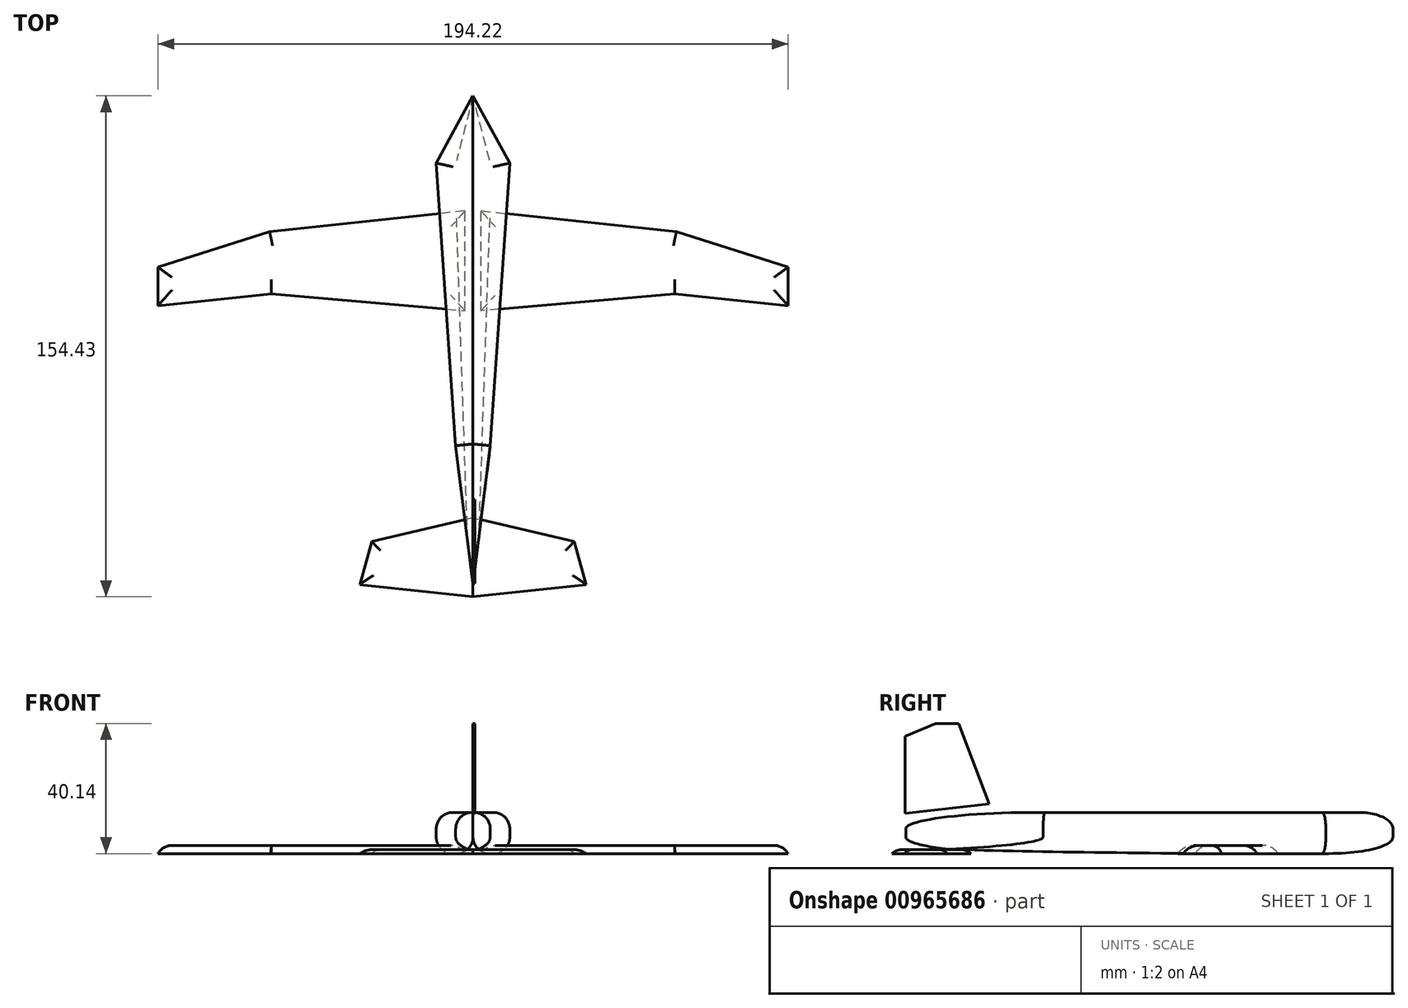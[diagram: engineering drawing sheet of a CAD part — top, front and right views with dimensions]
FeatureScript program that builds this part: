
annotation { "Feature Type Name" : "Feature", "Feature Type Description" : "" }
export const myFeature = defineFeature(function(context is Context, id is Id, definition is map)
    precondition{}
    {
        {
            var Q0;
            Q0=qCreatedBy(makeId("Top.planeOp"),FACE);
            var sketch = newSketch(context, id + "F0", { "sketchPlane" : qUnion([Q0])});
            skLineSegment(sketch, "E0", {"start": v(0, 25.84) * mm, "end": v(62.67, 19.1) * mm});
            skLineSegment(sketch, "E1", {"start": v(62.67, 19.1) * mm, "end": v(97.11, 8.22) * mm});
            skLineSegment(sketch, "E2", {"start": v(97.11, 8.22) * mm, "end": v(97.11, -3.66) * mm});
            skLineSegment(sketch, "E3", {"start": v(97.11, -3.66) * mm, "end": v(62.13, 0) * mm});
            skLineSegment(sketch, "E4", {"start": v(62.13, 0) * mm, "end": v(2.44, -5.26) * mm});
            skLineSegment(sketch, "E5", {"start": v(2.44, -5.26) * mm, "end": v(2.44, 25.84) * mm});
            skSolve(sketch);
        }
        {
            var Q0;
            {var subQ0=sQuery(id+"F0.wireOp",EDGE,"E1");Q0=makeQuery(id+"F0.imprint","IMPRINT",FACE,{"disambiguationData":[TD([[makeQuery(id+"F0.imprint","IMPRINT",EDGE,{"derivedFrom":subQ0}),-1.0]])]});}
            extrude(context, id + "F1", {"entities" : qUnion([Q0]), "depth" : 2.54 * mm, "offsetDistance" : 25.4 * mm});
        }
        {
            var Q0;
            Q0=makeQuery(id+"F1.opExtrude","CAP_EDGE",EDGE,{"disambiguationData":[OSD([sQuery(id+"F0.wireOp",EDGE,"E2")])],"isStart":false});
            var Q1;
            Q1=makeQuery(id+"F1.opExtrude","CAP_EDGE",EDGE,{"disambiguationData":[OSD([sQuery(id+"F0.wireOp",EDGE,"E1")])],"isStart":false});
            var Q2;
            Q2=makeQuery(id+"F1.opExtrude","CAP_FACE",FACE,{"disambiguationData":[OSD([sQuery(id+"F0.wireOp",EDGE,"E0"),sQuery(id+"F0.wireOp",EDGE,"E1"),sQuery(id+"F0.wireOp",EDGE,"E2"),sQuery(id+"F0.wireOp",EDGE,"E3"),sQuery(id+"F0.wireOp",EDGE,"E4"),sQuery(id+"F0.wireOp",EDGE,"E5")])],"isStart":false});
            fillet(context, id + "F2", {"entities" : qUnion([Q0, Q1, Q2]), "radius" : 5.08 * mm, "tangentPropagation" : true, "allowEdgeOverflow" : false});
        }
        {
            var Q0;
            Q0=qCreatedBy(makeId("Top.planeOp"),FACE);
            var sketch = newSketch(context, id + "F3", { "sketchPlane" : qUnion([Q0])});
            skLineSegment(sketch, "E6", {"start": v(0, -69.07) * mm, "end": v(31.2, -76.35) * mm});
            skLineSegment(sketch, "E7", {"start": v(31.2, -76.35) * mm, "end": v(34.91, -89.64) * mm});
            skLineSegment(sketch, "E8", {"start": v(34.91, -89.64) * mm, "end": v(0, -93.44) * mm});
            skLineSegment(sketch, "E9", {"start": v(0, -93.44) * mm, "end": v(0, -69.07) * mm});
            skSolve(sketch);
        }
        {
            var Q0;
            Q0=makeQuery(id+"F3.imprint","IMPRINT",FACE,{"disambiguationData":[TD([[makeQuery(id+"F3.imprint","IMPRINT",EDGE,{"derivedFrom":sQuery(id+"F3.wireOp",EDGE,"E6")}),-1.0]])]});
            extrude(context, id + "F4", {"entities" : qUnion([Q0]), "depth" : 1.27 * mm, "offsetDistance" : 25.4 * mm});
        }
        {
            var Q0;
            Q0=makeQuery(id+"F4.opExtrude","CAP_EDGE",EDGE,{"disambiguationData":[OSD([sQuery(id+"F3.wireOp",EDGE,"E7")])],"isStart":false});
            var Q1;
            Q1=makeQuery(id+"F4.opExtrude","CAP_EDGE",EDGE,{"disambiguationData":[OSD([sQuery(id+"F3.wireOp",EDGE,"E6")])],"isStart":false});
            var Q2;
            Q2=makeQuery(id+"F4.opExtrude","CAP_EDGE",EDGE,{"disambiguationData":[OSD([sQuery(id+"F3.wireOp",EDGE,"E8")])],"isStart":false});
            fillet(context, id + "F5", {"entities" : qUnion([Q0, Q1, Q2]), "radius" : 5.08 * mm, "tangentPropagation" : true, "allowEdgeOverflow" : false});
        }
        {
            var Q0;
            Q0=makeQuery(id+"F4.opExtrude","SWEPT_BODY",BODY,{"disambiguationData":[OSD([sQuery(id+"F3.wireOp",EDGE,"E6"),sQuery(id+"F3.wireOp",EDGE,"E7"),sQuery(id+"F3.wireOp",EDGE,"E8"),sQuery(id+"F3.wireOp",EDGE,"E9")])]});
            var Q1;
            Q1=qCreatedBy(makeId("Right.planeOp"),FACE);
            mirror(context, id + "F6", {"operationType" : NewBodyOperationType.ADD, "entities" : qUnion([Q0]), "mirrorPlane" : qUnion([Q1])});
        }
        {
            var Q0;
            Q0=makeQuery(id+"F1.opExtrude","SWEPT_BODY",BODY,{"disambiguationData":[OSD([sQuery(id+"F0.wireOp",EDGE,"E0"),sQuery(id+"F0.wireOp",EDGE,"E1"),sQuery(id+"F0.wireOp",EDGE,"E2"),sQuery(id+"F0.wireOp",EDGE,"E3"),sQuery(id+"F0.wireOp",EDGE,"E4"),sQuery(id+"F0.wireOp",EDGE,"E5")])]});
            var Q1;
            Q1=qCreatedBy(makeId("Right.planeOp"),FACE);
            mirror(context, id + "F7", {"entities" : qUnion([Q0]), "mirrorPlane" : qUnion([Q1])});
        }
        {
            var Q0;
            Q0=qCreatedBy(makeId("Top.planeOp"),FACE);
            var sketch = newSketch(context, id + "F8", { "sketchPlane" : qUnion([Q0])});
            skLineSegment(sketch, "E10", {"start": v(0, 61) * mm, "end": v(-11.34, 40.27) * mm});
            skLineSegment(sketch, "E11", {"start": v(-11.34, 40.27) * mm, "end": v(-5.33, -46.84) * mm});
            skLineSegment(sketch, "E12", {"start": v(-5.33, -46.84) * mm, "end": v(0, -89.2) * mm});
            skLineSegment(sketch, "E13", {"start": v(0, -89.2) * mm, "end": v(0, 61) * mm});
            skSolve(sketch);
        }
        {
            var Q0;
            Q0=makeQuery(id+"F8.imprint","IMPRINT",FACE,{"disambiguationData":[TD([[makeQuery(id+"F8.imprint","IMPRINT",EDGE,{"derivedFrom":sQuery(id+"F8.wireOp",EDGE,"E10")}),1.0]])]});
            extrude(context, id + "F9", {"entities" : qUnion([Q0]), "depth" : 12.7 * mm, "offsetDistance" : 25.4 * mm});
        }
        {
            var Q0;
            Q0=makeQuery(id+"F9.opExtrude","SWEPT_BODY",BODY,{"disambiguationData":[OSD([sQuery(id+"F8.wireOp",EDGE,"E10"),sQuery(id+"F8.wireOp",EDGE,"E11"),sQuery(id+"F8.wireOp",EDGE,"E12"),sQuery(id+"F8.wireOp",EDGE,"E13")])]});
            var Q1;
            Q1=qCreatedBy(makeId("Right.planeOp"),FACE);
            mirror(context, id + "F10", {"entities" : qUnion([Q0]), "mirrorPlane" : qUnion([Q1])});
        }
        {
            var Q0;
            Q0=makeQuery(id+"F9.opExtrude","CAP_EDGE",EDGE,{"disambiguationData":[OSD([sQuery(id+"F8.wireOp",EDGE,"E10")])],"isStart":false});
            var Q1;
            Q1=makeQuery(id+"F9.opExtrude","CAP_EDGE",EDGE,{"disambiguationData":[OSD([sQuery(id+"F8.wireOp",EDGE,"E11")])],"isStart":false});
            var Q2;
            Q2=makeQuery(id+"F9.opExtrude","CAP_EDGE",EDGE,{"disambiguationData":[OSD([sQuery(id+"F8.wireOp",EDGE,"E12")])],"isStart":false});
            var Q3;
            Q3=makeQuery(id+"F10.opPattern","COPY",EDGE,{"derivedFrom":makeQuery(id+"F9.opExtrude","CAP_EDGE",EDGE,{"disambiguationData":[OSD([sQuery(id+"F8.wireOp",EDGE,"E12")])],"isStart":false}),"instanceName":"1"});
            var Q4;
            Q4=makeQuery(id+"F10.opPattern","COPY",EDGE,{"derivedFrom":makeQuery(id+"F9.opExtrude","CAP_EDGE",EDGE,{"disambiguationData":[OSD([sQuery(id+"F8.wireOp",EDGE,"E11")])],"isStart":false}),"instanceName":"1"});
            var Q5;
            Q5=makeQuery(id+"F10.opPattern","COPY",EDGE,{"derivedFrom":makeQuery(id+"F9.opExtrude","CAP_EDGE",EDGE,{"disambiguationData":[OSD([sQuery(id+"F8.wireOp",EDGE,"E10")])],"isStart":false}),"instanceName":"1"});
            fillet(context, id + "F11", {"entities" : qUnion([Q0, Q1, Q2, Q3, Q4, Q5]), "radius" : 5.08 * mm, "tangentPropagation" : true, "allowEdgeOverflow" : false});
        }
        {
            var Q0;
            Q0=makeQuery(id+"F10.opPattern","COPY",EDGE,{"derivedFrom":makeQuery(id+"F9.opExtrude","CAP_EDGE",EDGE,{"disambiguationData":[OSD([sQuery(id+"F8.wireOp",EDGE,"E10")])],"isStart":true}),"instanceName":"1"});
            var Q1;
            Q1=makeQuery(id+"F9.opExtrude","CAP_EDGE",EDGE,{"disambiguationData":[OSD([sQuery(id+"F8.wireOp",EDGE,"E10")])],"isStart":true});
            var Q2;
            Q2=makeQuery(id+"F9.opExtrude","CAP_EDGE",EDGE,{"disambiguationData":[OSD([sQuery(id+"F8.wireOp",EDGE,"E11")])],"isStart":true});
            var Q3;
            Q3=makeQuery(id+"F10.opPattern","COPY",EDGE,{"derivedFrom":makeQuery(id+"F9.opExtrude","CAP_EDGE",EDGE,{"disambiguationData":[OSD([sQuery(id+"F8.wireOp",EDGE,"E11")])],"isStart":true}),"instanceName":"1"});
            var Q4;
            Q4=makeQuery(id+"F9.opExtrude","CAP_EDGE",EDGE,{"disambiguationData":[OSD([sQuery(id+"F8.wireOp",EDGE,"E12")])],"isStart":true});
            var Q5;
            Q5=makeQuery(id+"F10.opPattern","COPY",EDGE,{"derivedFrom":makeQuery(id+"F9.opExtrude","CAP_EDGE",EDGE,{"disambiguationData":[OSD([sQuery(id+"F8.wireOp",EDGE,"E12")])],"isStart":true}),"instanceName":"1"});
            var Q6;
            Q6=makeQuery(id+"F9.opExtrude","CAP_EDGE",EDGE,{"disambiguationData":[OSD([sQuery(id+"F8.wireOp",EDGE,"E13")])],"isStart":true});
            var Q7;
            Q7=makeQuery(id+"F10.opPattern","COPY",FACE,{"derivedFrom":makeQuery(id+"F9.opExtrude","CAP_FACE",FACE,{"disambiguationData":[OSD([sQuery(id+"F8.wireOp",EDGE,"E10"),sQuery(id+"F8.wireOp",EDGE,"E11"),sQuery(id+"F8.wireOp",EDGE,"E12"),sQuery(id+"F8.wireOp",EDGE,"E13")])],"isStart":true}),"instanceName":"1"});
            fillet(context, id + "F12", {"entities" : qUnion([Q0, Q1, Q2, Q3, Q4, Q5, Q6, Q7]), "radius" : 5.08 * mm, "tangentPropagation" : true, "allowEdgeOverflow" : false});
        }
        {
            var Q0;
            Q0=qCreatedBy(makeId("Right.planeOp"),FACE);
            var sketch = newSketch(context, id + "F13", { "sketchPlane" : qUnion([Q0])});
            skLineSegment(sketch, "E14", {"start": v(-89.37, 12.35) * mm, "end": v(-89.37, 36.1) * mm});
            skLineSegment(sketch, "E15", {"start": v(-89.37, 36.1) * mm, "end": v(-79.93, 40.14) * mm});
            skLineSegment(sketch, "E16", {"start": v(-79.93, 40.14) * mm, "end": v(-72.9, 40.14) * mm});
            skLineSegment(sketch, "E17", {"start": v(-72.9, 40.14) * mm, "end": v(-63.47, 15.31) * mm});
            skLineSegment(sketch, "E18", {"start": v(-63.47, 15.31) * mm, "end": v(-89.37, 12.35) * mm});
            skSolve(sketch);
        }
        {
            var Q0;
            Q0=makeQuery(id+"F13.imprint","IMPRINT",FACE,{"disambiguationData":[TD([[makeQuery(id+"F13.imprint","IMPRINT",EDGE,{"derivedFrom":sQuery(id+"F13.wireOp",EDGE,"E14")}),-1.0]])]});
            extrude(context, id + "F14", {"entities" : qUnion([Q0]), "depth" : 0.5 * mm, "offsetDistance" : 25.4 * mm});
        }
    });
